# Revit family: CADS_Vent-Axia_MechEquip_Fan_VSP_SabreSicklePlate_1Ph2P - EXTRACT
name_source: partatom
category: Mechanical Equipment
units: mm (PartAtom-declared; Revit-internal decimal feet)

## family parameters
Always vertical = Yes
Cut with Voids When Loaded = No
OmniClass Number = 23.75.00.00
OmniClass Title = Climate Control (HVAC)
Part Type = Normal
Room Calculation Point = No
Round Connector Dimension = Use Diameter
Shared = No
Work Plane-Based = No

## types (1)
- VSP25012A
    A = 370 mm  [stored 1.21391 ft]
    AirflowRateRange = 0.0 L/s
    AssemblyPlace = UNKNOWN
    AssetType = FIXED
    CADS_Index = 0
    CADS_Usage = 0
    Default Elevation = 0 mm  [stored 0 ft]
    DurationUnit = Year
    E = 34 mm
    ExpectedServiceLife = 0
    ExteriorInsulation = No
    Fitting Type = Ignore
    G = 17 mm
    GrossWeight = 0.00 kg
    HasProtectiveEarth = No
    IfcExportAs = IfcFanType
    IsExtendedWarranty = No
    ManufacturerAddress = Fleming Way
Crawley 
RH10 9YX
    ModelNumber = VSP25012A
    ModelReference = OWLET SICKLE PLATE FAN 250 DIA 1PH 2 POLE
    NominalDiameter = 250 mm  [stored 0.82021 ft]
    NominalHeight = 250 mm  [stored 0.82021 ft]
    NominalLength = 73 mm
    NominalWidth = 370 mm  [stored 1.21391 ft]
    NumberOfPoles = 0
    Quantity = 1
    RatedCurrent = 0 A
    RatedVoltage = 0 V
    Status = New
    WarrantyGuarantor = Vent-Axia Limited
    WorkingPressure = 0.0 Pa

note: [stored X ft] marks values corroborated as IEEE doubles in the binary element streams (Revit-internal decimal feet)

## geometry (parser evidence)
native form markers: Sweep x16
no freeform markers — native parametric forms only
